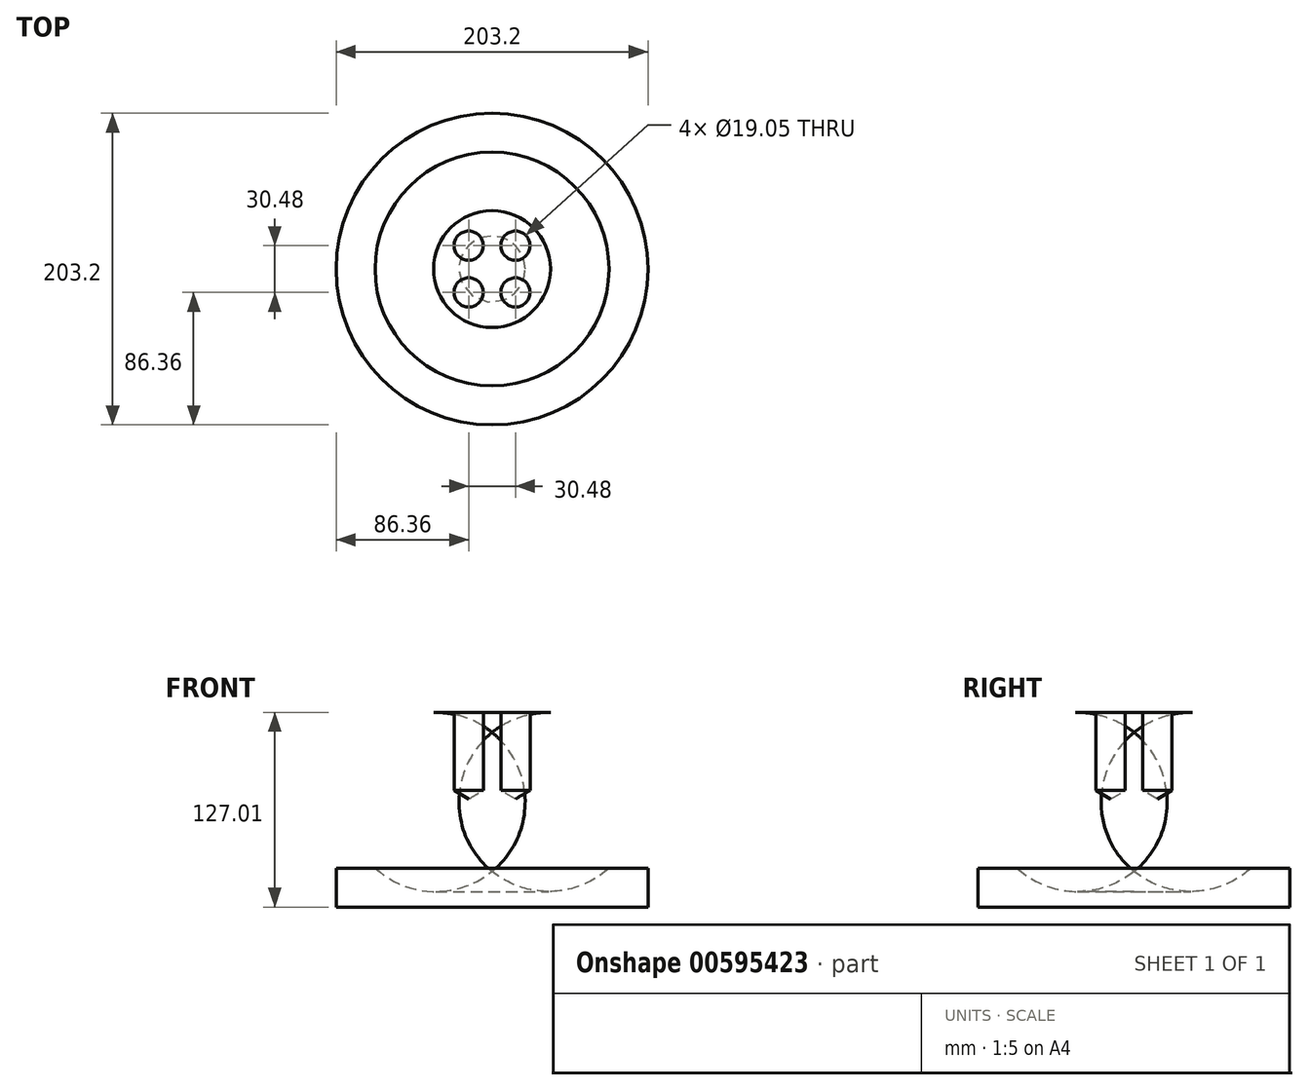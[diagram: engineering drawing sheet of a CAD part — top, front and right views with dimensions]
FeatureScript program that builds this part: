
annotation { "Feature Type Name" : "Feature", "Feature Type Description" : "" }
export const myFeature = defineFeature(function(context is Context, id is Id, definition is map)
    precondition{}
    {
        {
            var Q0;
            Q0=qCreatedBy(makeId("Front.planeOp"),FACE);
            var sketch = newSketch(context, id + "F0", { "sketchPlane" : qUnion([Q0])});
            skLineSegment(sketch, "E0", {"start": v(0, 0) * mm, "end": v(-101.6, 0) * mm});
            skLineSegment(sketch, "E1", {"start": v(-101.6, 0) * mm, "end": v(-101.6, 25.4) * mm});
            skLineSegment(sketch, "E2", {"start": v(-101.6, 25.4) * mm, "end": v(-76.2, 25.4) * mm});
            skLineSegment(sketch, "E3", {"start": v(0, 0) * mm, "end": v(0, 127) * mm});
            skLineSegment(sketch, "E4", {"start": v(0, 127) * mm, "end": v(-38.1, 127) * mm});
            skArc(sketch, "E5", {"start": v(-38.1, 127) * mm, "mid": v(-91.57, 89.1) * mm, "end": v(-76.2, 25.4) * mm});
            skSolve(sketch);
        }
        {
            var Q0;
            Q0=makeQuery(id+"F0.imprint","IMPRINT",FACE,{"disambiguationData":[TD([[makeQuery(id+"F0.imprint","IMPRINT",EDGE,{"derivedFrom":sQuery(id+"F0.wireOp",EDGE,"E0")}),-1.0]])]});
            var Q1;
            Q1=sQuery(id+"F0.wireOp",EDGE,"E3");
            revolve(context, id + "F1", {"entities" : qUnion([Q0]), "axis" : qUnion([Q1]), "revolveType" : RevolveType.FULL});
        }
        {
            var Q0;
            Q0=makeQuery(id+"F1.opRevolve","SWEPT_FACE",FACE,{"disambiguationData":[OSD([sQuery(id+"F0.wireOp",EDGE,"E4")])]});
            var sketch = newSketch(context, id + "F2", { "sketchPlane" : qUnion([Q0])});
            skCircle(sketch, "E6", {"center": v(-15.24, 15.24) * mm, "radius": 9.53 * mm});
            skLineSegment(sketch, "E7", {"start": v(0, 0) * mm, "end": v(-31.2, 0) * mm});
            skLineSegment(sketch, "E8", {"start": v(0, 0) * mm, "end": v(0, 31.04) * mm});
            skCircle(sketch, "E9.MirrorC", {"center": v(-15.24, -15.24) * mm, "radius": 9.53 * mm});
            skCircle(sketch, "E10.MirrorC", {"center": v(15.24, 15.24) * mm, "radius": 9.53 * mm});
            skLineSegment(sketch, "E11", {"start": v(0, 0) * mm, "end": v(30.22, 0) * mm});
            skCircle(sketch, "E12.MirrorC", {"center": v(15.24, -15.24) * mm, "radius": 9.53 * mm});
            skSolve(sketch);
        }
        {
            var Q0;
            Q0=sQuery(id+"F2.wireOp",VERTEX,"E6.center");
            var Q1;
            Q1=sQuery(id+"F2.wireOp",VERTEX,"E10.MirrorC.center");
            var Q2;
            Q2=sQuery(id+"F2.wireOp",VERTEX,"E12.MirrorC.center");
            var Q3;
            Q3=sQuery(id+"F2.wireOp",VERTEX,"E9.MirrorC.center");
            var Q4;
            Q4=makeQuery(id+"F1.opRevolve","SWEPT_BODY",BODY,{"disambiguationData":[OSD([sQuery(id+"F0.wireOp",EDGE,"E0"),sQuery(id+"F0.wireOp",EDGE,"E1"),sQuery(id+"F0.wireOp",EDGE,"E2"),sQuery(id+"F0.wireOp",EDGE,"E3"),sQuery(id+"F0.wireOp",EDGE,"E4"),sQuery(id+"F0.wireOp",EDGE,"E5")])]});
            hole(context, id + "F3", {"style" : HoleStyle.SIMPLE, "endStyle" : HoleEndStyle.BLIND, "holeDiameter" : 19.05 * mm, "majorDiameter" : 6.35 * mm, "holeDepth" : 50.8 * mm, "isTappedThrough" : true, "tappedDepth" : 12.7 * mm, "tapClearance" : 3, "locations" : qUnion([Q0, Q1, Q2, Q3]), "scope" : qUnion([Q4])});
        }
    });
